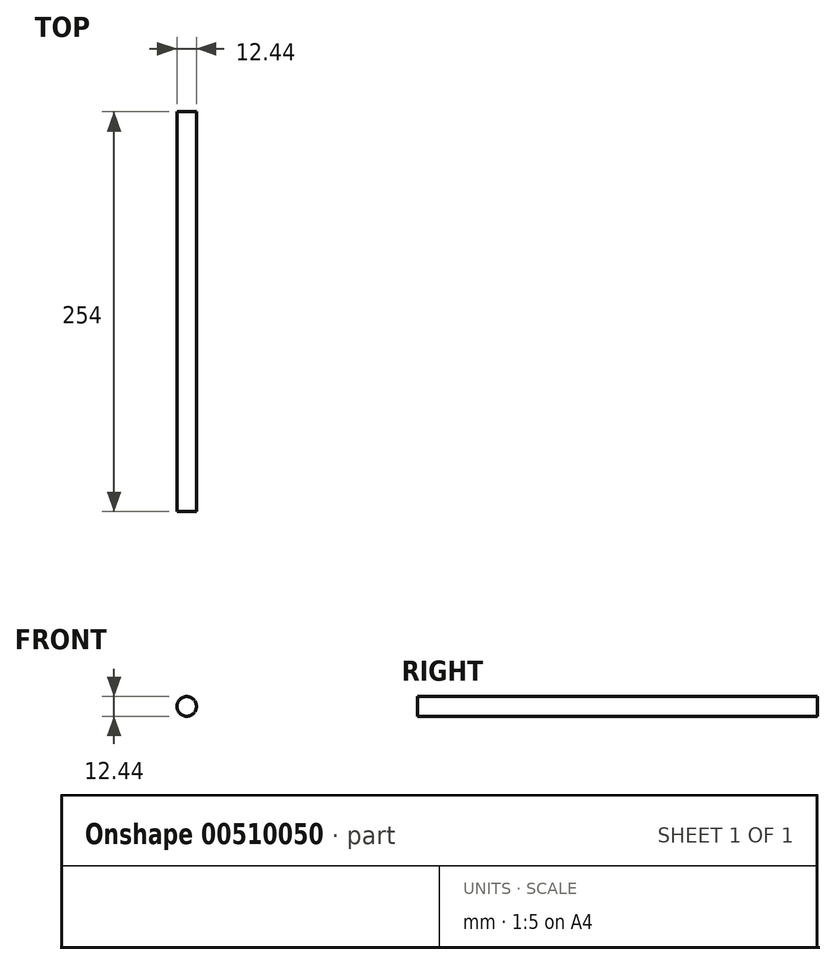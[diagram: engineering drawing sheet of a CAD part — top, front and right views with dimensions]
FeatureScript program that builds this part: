
annotation { "Feature Type Name" : "Feature", "Feature Type Description" : "" }
export const myFeature = defineFeature(function(context is Context, id is Id, definition is map)
    precondition{}
    {
        {
            var Q0;
            Q0=qCreatedBy(makeId("Front.planeOp"),FACE);
            var sketch = newSketch(context, id + "F0", { "sketchPlane" : qUnion([Q0])});
            skCircle(sketch, "E0", {"center": v(0, 0) * mm, "radius": 6.22 * mm});
            skSolve(sketch);
        }
        {
            var Q0;
            Q0=qSketchRegion(id+"F0",true);
            extrude(context, id + "F1", {"entities" : qUnion([Q0]), "depth" : 254 * mm});
        }
    });
